# Revit family: Faucet_Touchless-Wall_Mount-Lavatory-KOHLER-Oblo-K-8398T_1
name_source: partatom
category: Plumbing Fixtures
units: mm (PartAtom-declared; Revit-internal decimal feet)

## family parameters
Cut with Voids When Loaded = No
Host = Face
OmniClass Number = 23.31.11.00
OmniClass Title = Faucets
Part Type = Normal
Room Calculation Point = No
Round Connector Dimension = Use Diameter
Shared = No

## types (2) — shared parameters
ADA Compliant = No
Apparent Load = 0 VA
Assembly Code = D2010
CW Connection = Yes
Cold Water Inlet = Cold Water Inlet
Date Modified = 12/08/2022
Default Elevation = 36"
Drain Included = Yes
Electrical Connector = Yes
Electrical Note = One Dedicated Circuit Required
Finish = Kohler-Metal-CP-Polished_Chrome
Flow Rate = 1 GPM
HW Connection = No
Height = 2 5/16"
Hot Water Inlet = Hot Water Inlet
Length = 6 1/8"
Manufacturer = Kohler Co.
Master Format 2014 = 22 41 39
Master Format 2014 Name = Residential Faucets, Supplies, and Trim
Material = Brass Construction
Pressure = 60.00 psi
Product Documentation Link = https://files.kohler.com.cn
Product Name = Oblo
Product Page URL = https://www.kohler.com.cn
Spout Reach = 6 1/8"
URL = http://www.kohler.com.cn
Vent Connection = No
Voltage = 220 V
Waste Connection = No
Waste Water Outlet = Waste Water Outlet
WaterSense Certified = No
Width = 2 5/16"

## per-type parameters (varying)
| type | Description | Model | Type |
| Without Power Box, CP-Polished Chrome | wall outlet faucet single cooling, 1.9 liters (without power box) | K-8398T-NW-CP | 1 |
| With Power Box, CP-Polished Chrome | Wall water sensor faucet AC (single cooled type with AC power box) | K-8398T-CP | 2 |

## geometry (parser evidence)
native form markers: Sweep x5
no freeform markers — native parametric forms only
